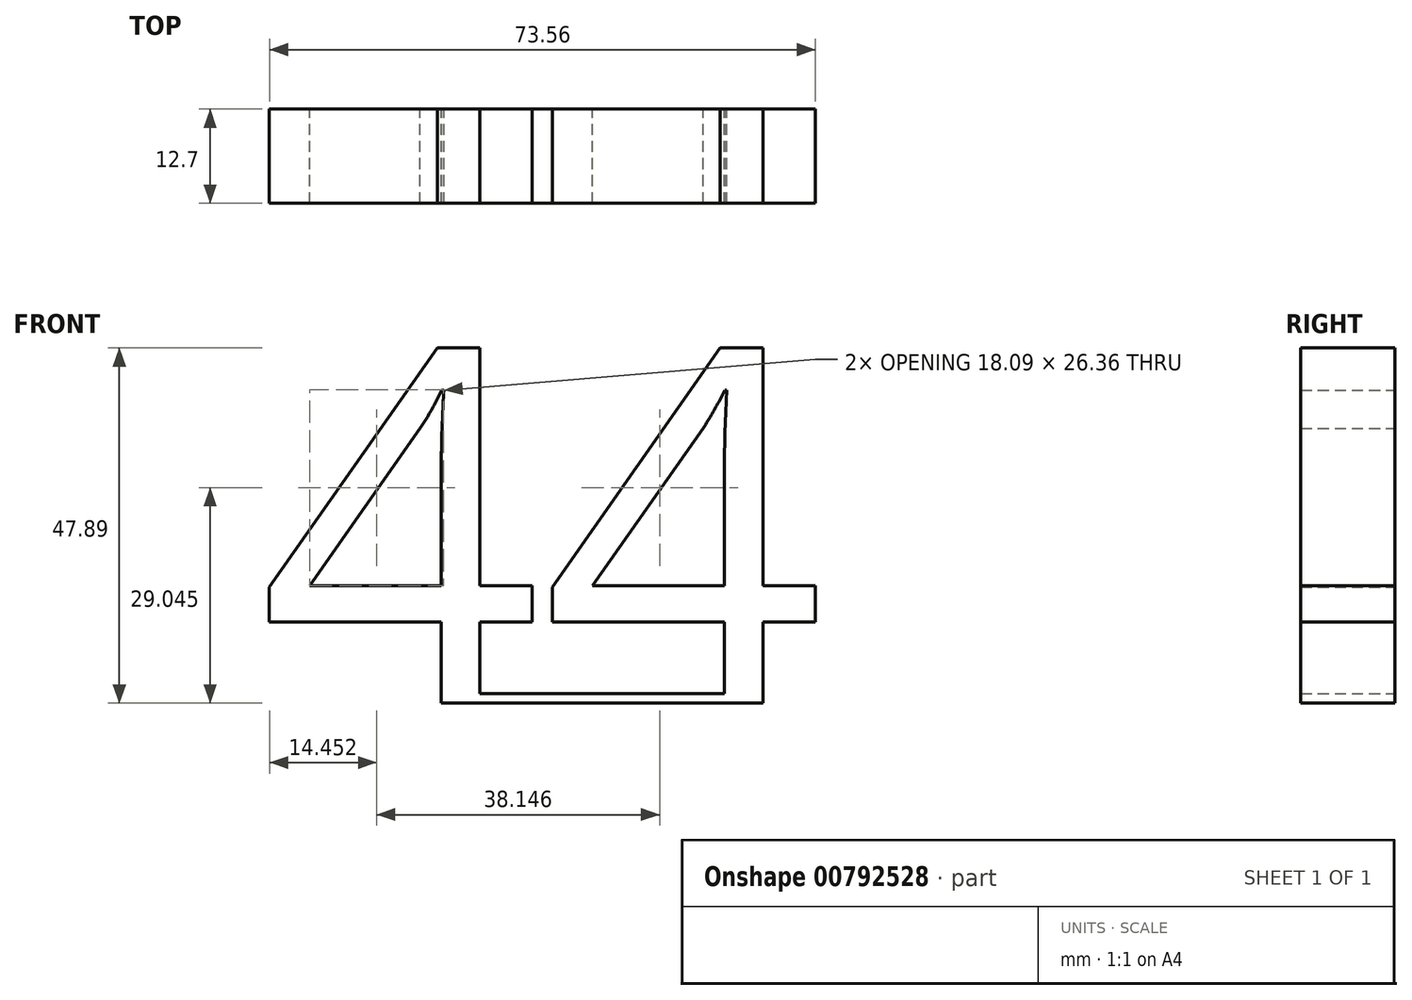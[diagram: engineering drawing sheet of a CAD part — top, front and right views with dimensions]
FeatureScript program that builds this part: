
annotation { "Feature Type Name" : "Feature", "Feature Type Description" : "" }
export const myFeature = defineFeature(function(context is Context, id is Id, definition is map)
    precondition{}
    {
        {
            var Q0;
            Q0=qCreatedBy(makeId("Front.planeOp"),FACE);
            var sketch = newSketch(context, id + "F0", { "sketchPlane" : qUnion([Q0])});
            skText(sketch, "E0", { "text": "44\n", "fontName": "OpenSans-Regular.ttf"});
            skLineSegment(sketch, "E1.bottom", {"start": v(-3.1, -48.04) * mm, "end": v(29.9, -48.04) * mm});
            skLineSegment(sketch, "E1.top", {"start": v(-3.1, -46.75) * mm, "end": v(29.9, -46.75) * mm});
            skLineSegment(sketch, "E1.left", {"start": v(-3.1, -48.04) * mm, "end": v(-3.1, -46.75) * mm});
            skLineSegment(sketch, "E1.right", {"start": v(29.9, -48.04) * mm, "end": v(29.9, -46.75) * mm});
            const initialGuessF0  = {"E0": [-0.03284, -0.04804, 1, 0, 0.04804]};
            skSetInitialGuess(sketch, initialGuessF0);
            skSolve(sketch);
        }
        {
            var Q0;
            Q0 = qSketchRegion(id + "F0", true);
            extrude(context, id + "F1", {"entities" : qUnion([Q0]), "depth" : 12.7 * mm, "offsetDistance" : 25.4 * mm});
        }
    });
